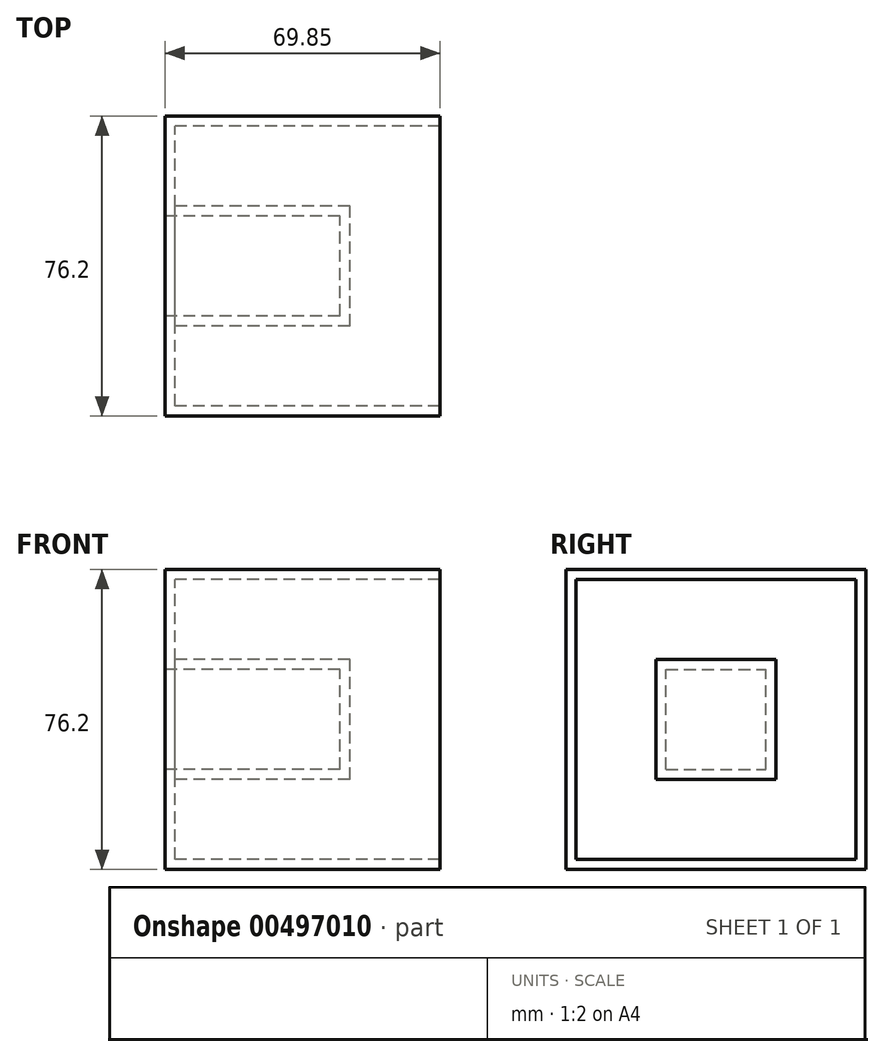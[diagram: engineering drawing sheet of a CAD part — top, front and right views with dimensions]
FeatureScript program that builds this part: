
annotation { "Feature Type Name" : "Feature", "Feature Type Description" : "" }
export const myFeature = defineFeature(function(context is Context, id is Id, definition is map)
    precondition{}
    {
        {
            var Q0;
            Q0=qCreatedBy(makeId("Right.planeOp"),FACE);
            var sketch = newSketch(context, id + "F0", { "sketchPlane" : qUnion([Q0])});
            skLineSegment(sketch, "E0.bottom", {"start": v(-38.1, -38.1) * mm, "end": v(38.1, -38.1) * mm});
            skLineSegment(sketch, "E0.top", {"start": v(-38.1, 38.1) * mm, "end": v(38.1, 38.1) * mm});
            skLineSegment(sketch, "E0.left", {"start": v(-38.1, -38.1) * mm, "end": v(-38.1, 38.1) * mm});
            skLineSegment(sketch, "E0.right", {"start": v(38.1, -38.1) * mm, "end": v(38.1, 38.1) * mm});
            skPoint(sketch, "E0.middle", {"position": v(0, 0) * mm});
            skSolve(sketch);
        }
        {
            var Q0;
            Q0=makeQuery(id+"F0.imprint","IMPRINT",FACE,{"disambiguationData":[TD([[makeQuery(id+"F0.imprint","IMPRINT",EDGE,{"derivedFrom":sQuery(id+"F0.wireOp",EDGE,"E0.bottom")}),1.0]])]});
            extrude(context, id + "F1", {"entities" : qUnion([Q0]), "depth" : 69.85 * mm});
        }
        {
            var Q0;
            Q0=makeQuery(id+"F1.opExtrude","CAP_FACE",FACE,{"disambiguationData":[OSD([sQuery(id+"F0.wireOp",EDGE,"E0.bottom"),sQuery(id+"F0.wireOp",EDGE,"E0.top"),sQuery(id+"F0.wireOp",EDGE,"E0.left"),sQuery(id+"F0.wireOp",EDGE,"E0.right")])],"isStart":true});
            shell(context, id + "F2", {"entities" : qUnion([Q0]), "thickness" : 25.4 * mm});
        }
        {
            var Q0;
            Q0=makeQuery(id+"F1.opExtrude","CAP_FACE",FACE,{"disambiguationData":[OSD([sQuery(id+"F0.wireOp",EDGE,"E0.bottom"),sQuery(id+"F0.wireOp",EDGE,"E0.top"),sQuery(id+"F0.wireOp",EDGE,"E0.left"),sQuery(id+"F0.wireOp",EDGE,"E0.right")])],"isStart":false});
            shell(context, id + "F3", {"entities" : qUnion([Q0]), "thickness" : 2.54 * mm});
        }
    });
